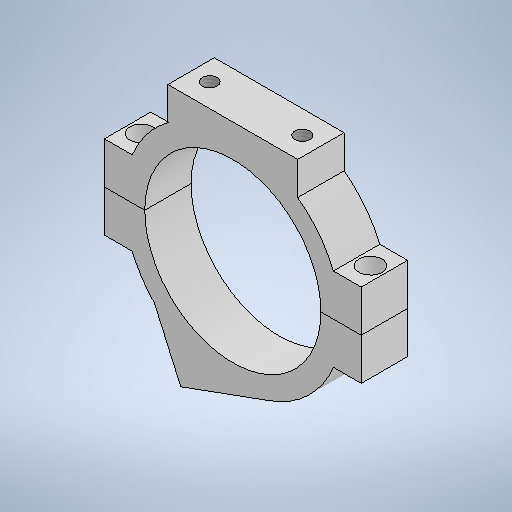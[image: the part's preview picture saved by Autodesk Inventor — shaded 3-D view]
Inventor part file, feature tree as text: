
AUTODESK INVENTOR PART (.ipt)
format: ipt  version: 2025 (Build 290162010, 162A)  size: 312,320 bytes
history: native  units: mm
features: sketch x5, hole x4, extrude x1, plane x1, split x1
ambient origin geometry x8: Origin, YZ Plane, XZ Plane, XY Plane, X Axis, Y Axis, Z Axis, Center Point
bodies: Solid1 (feature_tree)
feature tree (12):
  extrude  "Extrusion1"  Depth=47.0mm
  hole  "Hole1"  [1 undecoded]
  hole  "Hole2"  [1 undecoded]
  hole  "Hole3"  [1 undecoded]
  hole  "Hole4"  [1 undecoded]
  plane  "Work Plane1"
  split  "Split1"
  sketch  "Sketch1"  dims[d0=20.5mm d1=47.0mm]
  sketch  "Sketch2"  dims[d2=38.0mm d5=3.490659mm]
  sketch  "Sketch3"  dims[d7=14.0mm d8=18.0mm]
  sketch  "Sketch4"  dims[d9=6.0mm d10=28.0mm]
  sketch  "Sketch5"  dims[d11=18.0mm d14=10.0mm d15=0.0mm d17=3.0mm d18=6.0mm d19=5.0mm d20=5.0mm d21=90.0deg d22=9.5mm d23=0.0mm d24=6.0mm d25=5.0mm d26=6.0mm d27=5.0mm d28=5.0mm d29=90.0deg d30=9.5mm d31=0.0mm d32=6.0mm d33=17.0mm d34=5.0mm d35=6.0mm d36=4.0mm d37=2.0mm d38=90.0deg d39=8.0mm d40=0.0mm d41=3.242mm d42=6.0mm d43=4.0mm d44=2.0mm d45=90.0deg d46=6.0mm d47=0.0mm d48=4.0mm d49=4.0mm d50=0.0mm]
note: 4 required parameter values undecoded (feature->parameter linkage not recoverable at this tier; creation-order binding heuristic only, values carry confidence <= 0.55)
